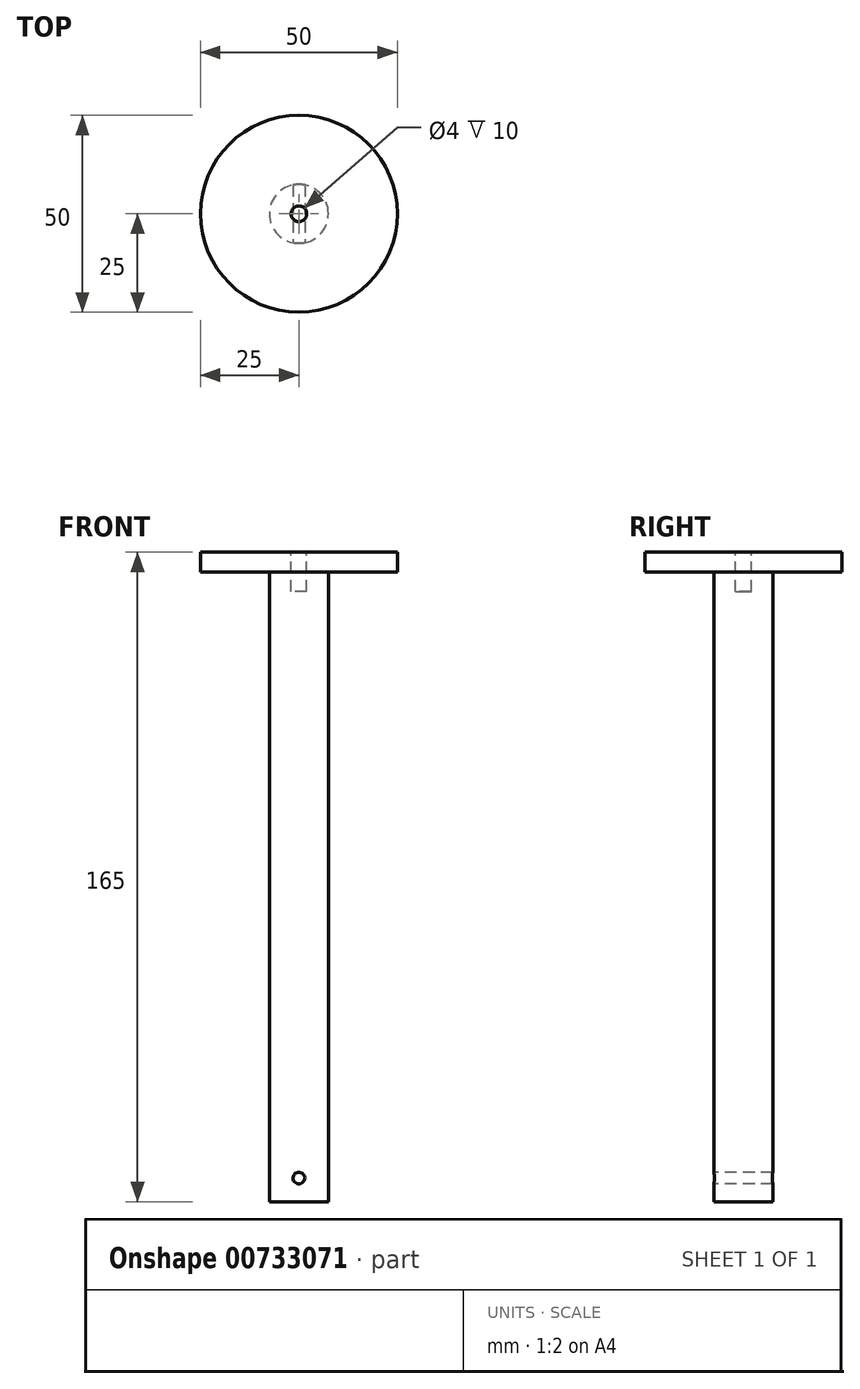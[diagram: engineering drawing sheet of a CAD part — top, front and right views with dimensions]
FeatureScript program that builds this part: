
annotation { "Feature Type Name" : "Feature", "Feature Type Description" : "" }
export const myFeature = defineFeature(function(context is Context, id is Id, definition is map)
    precondition{}
    {
        {
            var Q0;
            Q0=qCreatedBy(makeId("Top.planeOp"),FACE);
            var sketch = newSketch(context, id + "F0", { "sketchPlane" : qUnion([Q0])});
            skCircle(sketch, "E0", {"center": v(0, 0) * mm, "radius": 7.5 * mm});
            skSolve(sketch);
        }
        {
            var Q0;
            Q0=qSketchRegion(id+"F0",true);
            extrude(context, id + "F1", {"entities" : qUnion([Q0]), "depth" : 160 * mm, "offsetDistance" : 25 * mm});
        }
        {
            var Q0;
            Q0=makeQuery(id+"F1.opExtrude","CAP_FACE",FACE,{"disambiguationData":[OSD([sQuery(id+"F0.wireOp",EDGE,"E0")])],"isStart":false});
            var sketch = newSketch(context, id + "F2", { "sketchPlane" : qUnion([Q0])});
            skCircle(sketch, "E1", {"center": v(0, 0) * mm, "radius": 25 * mm});
            skSolve(sketch);
        }
        {
            var Q0;
            Q0=qSketchRegion(id+"F2",true);
            extrude(context, id + "F3", {"entities" : qUnion([Q0]), "operationType" : NewBodyOperationType.ADD, "depth" : 5 * mm, "offsetDistance" : 25 * mm});
        }
        {
            var Q0;
            Q0=qCreatedBy(makeId("Front.planeOp"),FACE);
            var sketch = newSketch(context, id + "F4", { "sketchPlane" : qUnion([Q0])});
            skCircle(sketch, "E2", {"center": v(0, 6) * mm, "radius": 1.5 * mm});
            skSolve(sketch);
        }
        {
            var Q0;
            Q0=qSketchRegion(id+"F4",true);
            extrude(context, id + "F5", {"entities" : qUnion([Q0]), "operationType" : NewBodyOperationType.REMOVE, "endBound" : BoundingType.UP_TO_NEXT, "oppositeDirection" : true, "depth" : 25 * mm, "offsetDistance" : 25 * mm, "hasSecondDirection" : true, "secondDirectionBound" : SecondDirectionBoundingType.UP_TO_NEXT, "secondDirectionOppositeDirection" : false, "secondDirectionDepth" : 25 * mm});
        }
        {
            var Q0;
            Q0=makeQuery(id+"F3.opExtrude","CAP_FACE",FACE,{"disambiguationData":[OSD([sQuery(id+"F2.wireOp",EDGE,"E1")])],"isStart":false});
            var sketch = newSketch(context, id + "F6", { "sketchPlane" : qUnion([Q0])});
            skCircle(sketch, "E3", {"center": v(0, 0) * mm, "radius": 2 * mm});
            skSolve(sketch);
        }
        {
            var Q0;
            Q0=qSketchRegion(id+"F6",true);
            extrude(context, id + "F7", {"entities" : qUnion([Q0]), "operationType" : NewBodyOperationType.REMOVE, "oppositeDirection" : true, "depth" : 10 * mm, "offsetDistance" : 25 * mm});
        }
    });
